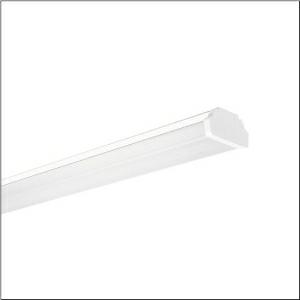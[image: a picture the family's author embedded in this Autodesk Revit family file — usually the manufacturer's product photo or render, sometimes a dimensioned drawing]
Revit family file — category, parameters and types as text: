
# Revit family: dus_31_gen_2_53bd812mv4a5c2_35bc
name_source: partatom
category: Lighting Fixtures
units: mm (PartAtom-declared; Revit-internal decimal feet)

## family parameters
Cut with Voids When Loaded = No
Host = Face
Light Source = No
Part Type = Normal
Room Calculation Point = No
Round Connector Dimension = Use Diameter
Shared = No

## types (1)
- --- (1 x LED, 10960 lm, 60.5 W, 4000K)
    Apparent Load = 61 VA
    CIE Flux Codes = 47 80 95 93 100
    Color Rendering = 80
    Color Temperature = 4000K
    Default Elevation = 1800 mm
    Description = DUS 31 Gen.2, luminaire insert, of sheet steel, coil coated, white, length: 1.535mm, width: 81mm, height: 90mm, 5x system unit, system units: 307mm, LED rated luminous flux: 10.960lm, light colour: 840, SDCM (Standard Deviation of Colour Matching)MacAdam ≤ 3 SDCM (initial), control gear: ON/OFF Multilumen, control gear: ECG, with plug, 3-pole, with phase selection, mains connection: 220..240V, AC, 50/60Hz, rated input power: 61W, through-wiring accessed according to module size, primary optical cover: cover, of PMMA, light emission: direct distribution, primary light characteristic: symmetric, protection rating (complete): IP20, protection rating (LED compartment): IP50, insulation class (complete): insulation class I (protective earthing), certification: CE, ENEC, VDE, UKCA, impact resistance: IK03, permissible ambient temperature for indoor applications: -35..+40°C, corresponds to IFS (International Featured Standards) requirements for safety and quality in the food industry, reducing of maximum allowable ambient temperature of 5°C with ceiling mounting, packaging unit: 1 piece
    Height = 95 mm
    Lamp = 1 x LED
    Lamp Light Flux = 10960 lm
    Lamp Power = 60.5 W
    Lamp count = 1
    Length = 1535 mm
    Luminous efficacy = 181 lm/W
    Manufacturer = Siteco
    ModVariant = No
    Model = 53BD812MV4A5C2
    Mounting Place = Ceiling
    Mounting Type = Pendant
    Number of Poles = 1
    OnlyDefault = Yes
    Power Factor = 1
    Product Name = DUS 31 Gen.2
    Product group = luminaire insert | ceiling pendant
    ProductGroupID = 901
    Protection Class = Protection class I
    Protection Degree = IP 20
    RLX_Detail_Level = 1
    RLX_Emergency_Light_Flux = 0 lm
    RLX_Emergency_Type = 0
    RLX_Emergency_Type_DB = No
    RlxData = <blob elided: 29801 chars, md5=88bfdeb7>
    Socket = socket
    Standby Power = 0 W
    System Light Flux = 10960 lm
    System Power = 61 W
    Type Comments = factory setting: luminous flux: 100 % | (A | C | E) | 140 mA
    Type Image = l_1319596.jpg
    URL = http://relux.com
    VarID = @adj_049725
    Voltage = 0 V
    Weight = 0.00 kg
    Width = 81 mm

## geometry (parser evidence)
native form markers: Blend x4, Sweep x14
no freeform markers — native parametric forms only
